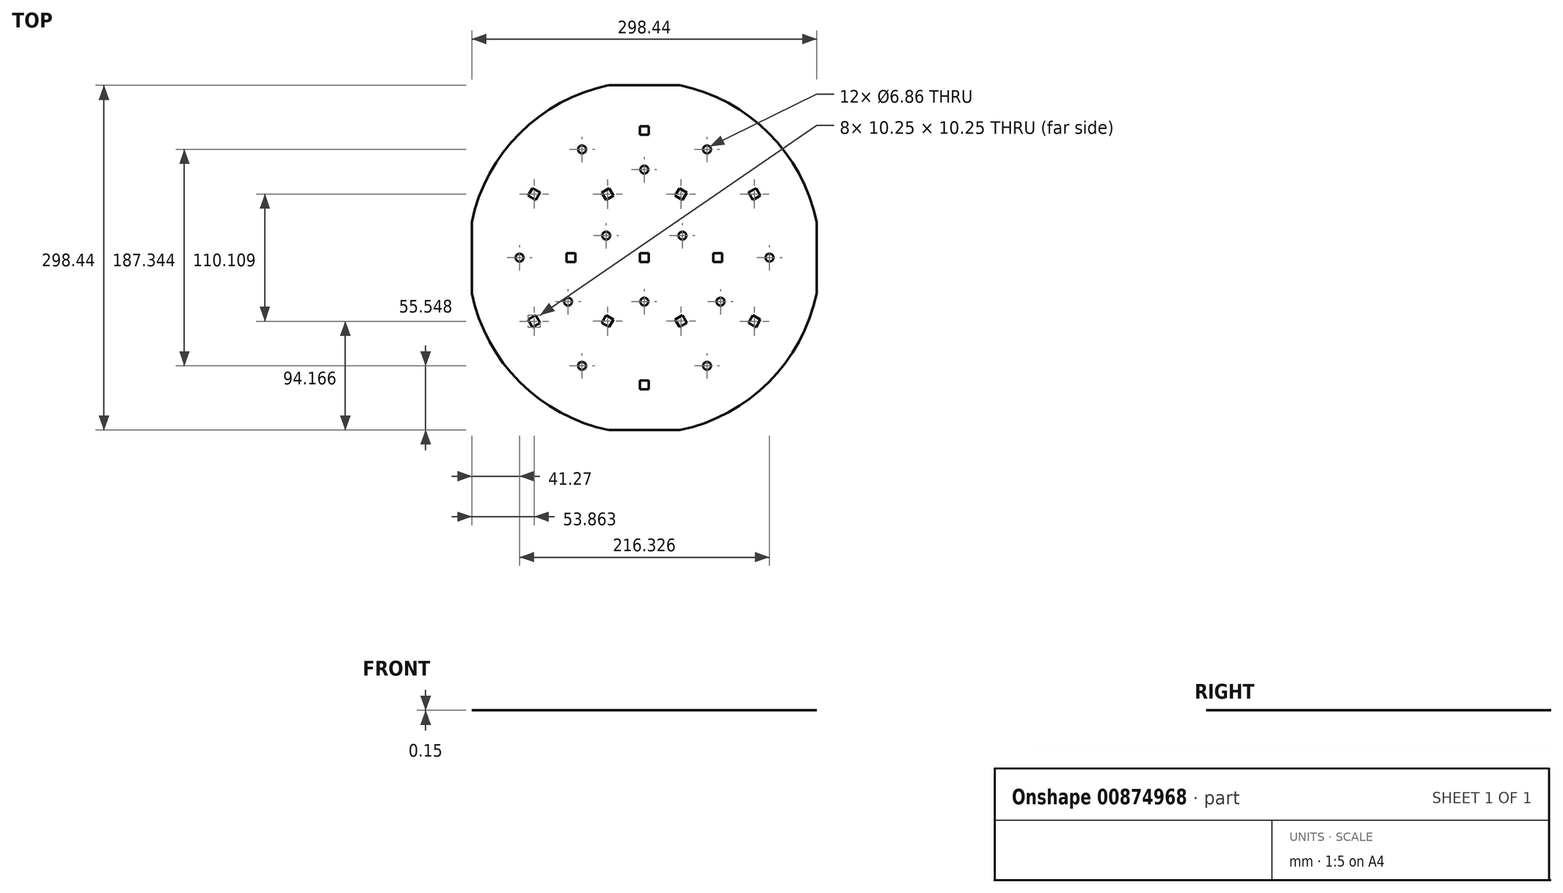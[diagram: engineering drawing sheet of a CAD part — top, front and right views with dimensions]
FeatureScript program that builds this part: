
annotation { "Feature Type Name" : "Feature", "Feature Type Description" : "" }
export const myFeature = defineFeature(function(context is Context, id is Id, definition is map)
    precondition{}
    {
        {
            var Q0;
            Q0=qCreatedBy(makeId("Top.planeOp"),FACE);
            var sketch = newSketch(context, id + "F0", { "sketchPlane" : qUnion([Q0])});
            skCircle(sketch, "E0", {"center": v(0, 0) * mm, "radius": 152.4 * mm});
            skSolve(sketch);
        }
        {
            var Q0;
            Q0 = qSketchRegion(id + "F0", true);
            extrude(context, id + "F1", {"entities" : qUnion([Q0]), "depth" : 0.15 * mm, "offsetDistance" : 25.4 * mm});
        }
        {
            var Q0;
            Q0=makeQuery(id+"F1.opExtrude","CAP_FACE",FACE,{"disambiguationData":[OSD([sQuery(id+"F0.wireOp",EDGE,"E0")])],"isStart":false});
            var sketch = newSketch(context, id + "F2", { "sketchPlane" : qUnion([Q0])});
            skLineSegment(sketch, "E1.bottom", {"start": v(-161.93, -63.5) * mm, "end": v(-149.23, -63.5) * mm});
            skLineSegment(sketch, "E1.top", {"start": v(-161.93, 63.5) * mm, "end": v(-149.23, 63.5) * mm});
            skLineSegment(sketch, "E1.left", {"start": v(-161.92, -63.5) * mm, "end": v(-161.92, 63.5) * mm});
            skLineSegment(sketch, "E1.right", {"start": v(-149.23, -63.5) * mm, "end": v(-149.23, 63.5) * mm});
            skLineSegment(sketch, "E2.bottom", {"start": v(-63.5, -161.92) * mm, "end": v(63.5, -161.92) * mm});
            skLineSegment(sketch, "E2.top", {"start": v(-63.5, -149.23) * mm, "end": v(63.5, -149.23) * mm});
            skLineSegment(sketch, "E2.left", {"start": v(-63.5, -161.92) * mm, "end": v(-63.5, -149.23) * mm});
            skLineSegment(sketch, "E2.right", {"start": v(63.5, -161.92) * mm, "end": v(63.5, -149.23) * mm});
            skLineSegment(sketch, "E3.bottom", {"start": v(-63.5, 161.93) * mm, "end": v(63.5, 161.93) * mm});
            skLineSegment(sketch, "E3.top", {"start": v(-63.5, 149.23) * mm, "end": v(63.5, 149.23) * mm});
            skLineSegment(sketch, "E3.left", {"start": v(-63.5, 161.93) * mm, "end": v(-63.5, 149.23) * mm});
            skLineSegment(sketch, "E3.right", {"start": v(63.5, 161.93) * mm, "end": v(63.5, 149.23) * mm});
            skLineSegment(sketch, "E4.bottom", {"start": v(149.23, -63.5) * mm, "end": v(161.93, -63.5) * mm});
            skLineSegment(sketch, "E4.top", {"start": v(149.23, 63.5) * mm, "end": v(161.93, 63.5) * mm});
            skLineSegment(sketch, "E4.left", {"start": v(149.23, -63.5) * mm, "end": v(149.23, 63.5) * mm});
            skLineSegment(sketch, "E4.right", {"start": v(161.92, -63.5) * mm, "end": v(161.92, 63.5) * mm});
            skSolve(sketch);
        }
        {
            var Q0;
            Q0 = qSketchRegion(id + "F2", true);
            extrude(context, id + "F3", {"entities" : qUnion([Q0]), "operationType" : NewBodyOperationType.REMOVE, "oppositeDirection" : true, "depth" : 25.4 * mm, "offsetDistance" : 25.4 * mm});
        }
        {
            var Q0;
            Q0=makeQuery(id+"F1.opExtrude","CAP_FACE",FACE,{"disambiguationData":[OSD([sQuery(id+"F0.wireOp",EDGE,"E0")])],"isStart":false});
            var sketch = newSketch(context, id + "F4", { "sketchPlane" : qUnion([Q0])});
            skPoint(sketch, "E5", {"position": v(-107.95, 0) * mm});
            skPoint(sketch, "E6", {"position": v(0, 76.2) * mm});
            skPoint(sketch, "E7", {"position": v(0, -38.1) * mm});
            skPoint(sketch, "E8.1.0", {"position": v(-53.87, -93.67) * mm});
            skPoint(sketch, "E8.2.0", {"position": v(54.3, -93.67) * mm});
            skPoint(sketch, "E8.3.0", {"position": v(108.38, 0) * mm});
            skPoint(sketch, "E8.4.0", {"position": v(54.3, 93.67) * mm});
            skPoint(sketch, "E8.5.0", {"position": v(-53.87, 93.67) * mm});
            skPoint(sketch, "E8.center", {"position": v(0.21, 0) * mm});
            skLineSegment(sketch, "E8.anchor1", {"start": v(0.21, 0) * mm, "end": v(-107.95, 0) * mm, "construction": true});
            skLineSegment(sketch, "E8.anchor2", {"start": v(0.21, 0) * mm, "end": v(-53.87, 93.67) * mm, "construction": true});
            skPoint(sketch, "E9.1.0", {"position": v(-66, -38.1) * mm});
            skPoint(sketch, "E9.2.0", {"position": v(66, -38.1) * mm});
            skPoint(sketch, "E9.center", {"position": v(0, 0) * mm});
            skPoint(sketch, "E10.1.0", {"position": v(33, 19.05) * mm});
            skPoint(sketch, "E10.2.0", {"position": v(-33, 19.05) * mm});
            skSolve(sketch);
        }
        {
            var Q0;
            Q0=sQuery(id+"F4.wireOp",VERTEX,"E8.1.0");
            var Q1;
            Q1=sQuery(id+"F4.wireOp",VERTEX,"E8.2.0");
            var Q2;
            Q2=sQuery(id+"F4.wireOp",VERTEX,"E9.2.0");
            var Q3;
            Q3=sQuery(id+"F4.wireOp",VERTEX,"E7");
            var Q4;
            Q4=sQuery(id+"F4.wireOp",VERTEX,"E9.1.0");
            var Q5;
            Q5=sQuery(id+"F4.wireOp",VERTEX,"E5");
            var Q6;
            Q6=sQuery(id+"F4.wireOp",VERTEX,"E10.2.0");
            var Q7;
            Q7=sQuery(id+"F4.wireOp",VERTEX,"E10.1.0");
            var Q8;
            Q8=sQuery(id+"F4.wireOp",VERTEX,"E8.3.0");
            var Q9;
            Q9=sQuery(id+"F4.wireOp",VERTEX,"E6");
            var Q10;
            Q10=sQuery(id+"F4.wireOp",VERTEX,"E8.4.0");
            var Q11;
            Q11=sQuery(id+"F4.wireOp",VERTEX,"E8.5.0");
            var Q12;
            Q12=makeQuery(id+"F1.opExtrude","SWEPT_BODY",BODY,{"disambiguationData":[OSD([sQuery(id+"F0.wireOp",EDGE,"E0")])]});
            hole(context, id + "F5", {"style" : HoleStyle.SIMPLE, "endStyle" : HoleEndStyle.THROUGH, "holeDiameter" : 6.86 * mm, "majorDiameter" : 6.35 * mm, "isTappedThrough" : true, "tappedDepth" : 12.7 * mm, "tapClearance" : 3, "locations" : qUnion([Q0, Q1, Q2, Q3, Q4, Q5, Q6, Q7, Q8, Q9, Q10, Q11]), "scope" : qUnion([Q12])});
        }
        {
            var Q0;
            Q0=makeQuery(id+"F1.opExtrude","CAP_FACE",FACE,{"disambiguationData":[OSD([sQuery(id+"F0.wireOp",EDGE,"E0")])],"isStart":false});
            var sketch = newSketch(context, id + "F6", { "sketchPlane" : qUnion([Q0])});
            skLineSegment(sketch, "E11.bottom", {"start": v(-3.75, -3.75) * mm, "end": v(3.75, -3.75) * mm});
            skLineSegment(sketch, "E11.top", {"start": v(-3.75, 3.75) * mm, "end": v(3.75, 3.75) * mm});
            skLineSegment(sketch, "E11.left", {"start": v(-3.75, -3.75) * mm, "end": v(-3.75, 3.75) * mm});
            skLineSegment(sketch, "E11.right", {"start": v(3.75, -3.75) * mm, "end": v(3.75, 3.75) * mm});
            skLineSegment(sketch, "E12.bottom", {"start": v(-67.25, -3.75) * mm, "end": v(-59.75, -3.75) * mm});
            skLineSegment(sketch, "E12.top", {"start": v(-67.25, 3.75) * mm, "end": v(-59.75, 3.75) * mm});
            skLineSegment(sketch, "E12.left", {"start": v(-67.25, -3.75) * mm, "end": v(-67.25, 3.75) * mm});
            skLineSegment(sketch, "E12.right", {"start": v(-59.75, -3.75) * mm, "end": v(-59.75, 3.75) * mm});
            skLineSegment(sketch, "E13.bottom", {"start": v(-3.75, 106.36) * mm, "end": v(3.75, 106.36) * mm});
            skLineSegment(sketch, "E13.top", {"start": v(-3.75, 113.86) * mm, "end": v(3.75, 113.86) * mm});
            skLineSegment(sketch, "E13.left", {"start": v(-3.75, 106.36) * mm, "end": v(-3.75, 113.86) * mm});
            skLineSegment(sketch, "E13.right", {"start": v(3.75, 106.36) * mm, "end": v(3.75, 113.86) * mm});
            skLineSegment(sketch, "E14.1.0", {"start": v(-30.38, -60.11) * mm, "end": v(-26.63, -53.62) * mm});
            skLineSegment(sketch, "E14.1.1", {"start": v(-26.63, -53.62) * mm, "end": v(-33.12, -49.87) * mm});
            skLineSegment(sketch, "E14.1.2", {"start": v(-36.87, -56.36) * mm, "end": v(-33.12, -49.87) * mm});
            skLineSegment(sketch, "E14.1.3", {"start": v(-30.38, -60.11) * mm, "end": v(-36.87, -56.36) * mm});
            skLineSegment(sketch, "E14.2.0", {"start": v(36.87, -56.36) * mm, "end": v(33.12, -49.87) * mm});
            skLineSegment(sketch, "E14.2.1", {"start": v(33.12, -49.87) * mm, "end": v(26.63, -53.62) * mm});
            skLineSegment(sketch, "E14.2.2", {"start": v(30.38, -60.11) * mm, "end": v(26.63, -53.62) * mm});
            skLineSegment(sketch, "E14.2.3", {"start": v(36.87, -56.36) * mm, "end": v(30.38, -60.11) * mm});
            skLineSegment(sketch, "E14.3.0", {"start": v(67.25, 3.75) * mm, "end": v(59.75, 3.75) * mm});
            skLineSegment(sketch, "E14.3.1", {"start": v(59.75, 3.75) * mm, "end": v(59.75, -3.75) * mm});
            skLineSegment(sketch, "E14.3.2", {"start": v(67.25, -3.75) * mm, "end": v(59.75, -3.75) * mm});
            skLineSegment(sketch, "E14.3.3", {"start": v(67.25, 3.75) * mm, "end": v(67.25, -3.75) * mm});
            skLineSegment(sketch, "E14.4.0", {"start": v(30.38, 60.11) * mm, "end": v(26.63, 53.62) * mm});
            skLineSegment(sketch, "E14.4.1", {"start": v(26.63, 53.62) * mm, "end": v(33.12, 49.87) * mm});
            skLineSegment(sketch, "E14.4.2", {"start": v(36.87, 56.36) * mm, "end": v(33.12, 49.87) * mm});
            skLineSegment(sketch, "E14.4.3", {"start": v(30.38, 60.11) * mm, "end": v(36.87, 56.36) * mm});
            skLineSegment(sketch, "E14.5.0", {"start": v(-36.87, 56.36) * mm, "end": v(-33.12, 49.87) * mm});
            skLineSegment(sketch, "E14.5.1", {"start": v(-33.12, 49.87) * mm, "end": v(-26.63, 53.62) * mm});
            skLineSegment(sketch, "E14.5.2", {"start": v(-30.38, 60.11) * mm, "end": v(-26.63, 53.62) * mm});
            skLineSegment(sketch, "E14.5.3", {"start": v(-36.87, 56.36) * mm, "end": v(-30.38, 60.11) * mm});
            skPoint(sketch, "E14.center", {"position": v(0, 0) * mm});
            skLineSegment(sketch, "E15.1.0", {"start": v(-93.98, 49.93) * mm, "end": v(-90.23, 56.43) * mm});
            skLineSegment(sketch, "E15.1.1", {"start": v(-90.23, 56.43) * mm, "end": v(-96.73, 60.18) * mm});
            skLineSegment(sketch, "E15.1.2", {"start": v(-93.98, 49.93) * mm, "end": v(-100.48, 53.68) * mm});
            skLineSegment(sketch, "E15.1.3", {"start": v(-100.48, 53.68) * mm, "end": v(-96.73, 60.18) * mm});
            skLineSegment(sketch, "E15.2.0", {"start": v(-90.23, -56.43) * mm, "end": v(-93.98, -49.93) * mm});
            skLineSegment(sketch, "E15.2.1", {"start": v(-93.98, -49.93) * mm, "end": v(-100.48, -53.68) * mm});
            skLineSegment(sketch, "E15.2.2", {"start": v(-90.23, -56.43) * mm, "end": v(-96.73, -60.18) * mm});
            skLineSegment(sketch, "E15.2.3", {"start": v(-96.73, -60.18) * mm, "end": v(-100.48, -53.68) * mm});
            skLineSegment(sketch, "E15.3.0", {"start": v(3.75, -106.36) * mm, "end": v(-3.75, -106.36) * mm});
            skLineSegment(sketch, "E15.3.1", {"start": v(-3.75, -106.36) * mm, "end": v(-3.75, -113.86) * mm});
            skLineSegment(sketch, "E15.3.2", {"start": v(3.75, -106.36) * mm, "end": v(3.75, -113.86) * mm});
            skLineSegment(sketch, "E15.3.3", {"start": v(3.75, -113.86) * mm, "end": v(-3.75, -113.86) * mm});
            skLineSegment(sketch, "E15.4.0", {"start": v(93.98, -49.93) * mm, "end": v(90.23, -56.43) * mm});
            skLineSegment(sketch, "E15.4.1", {"start": v(90.23, -56.43) * mm, "end": v(96.73, -60.18) * mm});
            skLineSegment(sketch, "E15.4.2", {"start": v(93.98, -49.93) * mm, "end": v(100.48, -53.68) * mm});
            skLineSegment(sketch, "E15.4.3", {"start": v(100.48, -53.68) * mm, "end": v(96.73, -60.18) * mm});
            skLineSegment(sketch, "E15.5.0", {"start": v(90.23, 56.43) * mm, "end": v(93.98, 49.93) * mm});
            skLineSegment(sketch, "E15.5.1", {"start": v(93.98, 49.93) * mm, "end": v(100.48, 53.68) * mm});
            skLineSegment(sketch, "E15.5.2", {"start": v(90.23, 56.43) * mm, "end": v(96.73, 60.18) * mm});
            skLineSegment(sketch, "E15.5.3", {"start": v(96.73, 60.18) * mm, "end": v(100.48, 53.68) * mm});
            skSolve(sketch);
        }
        {
            var Q0;
            Q0 = qSketchRegion(id + "F6", true);
            extrude(context, id + "F7", {"entities" : qUnion([Q0]), "operationType" : NewBodyOperationType.REMOVE, "oppositeDirection" : true, "depth" : 25.4 * mm, "offsetDistance" : 25.4 * mm});
        }
    });
